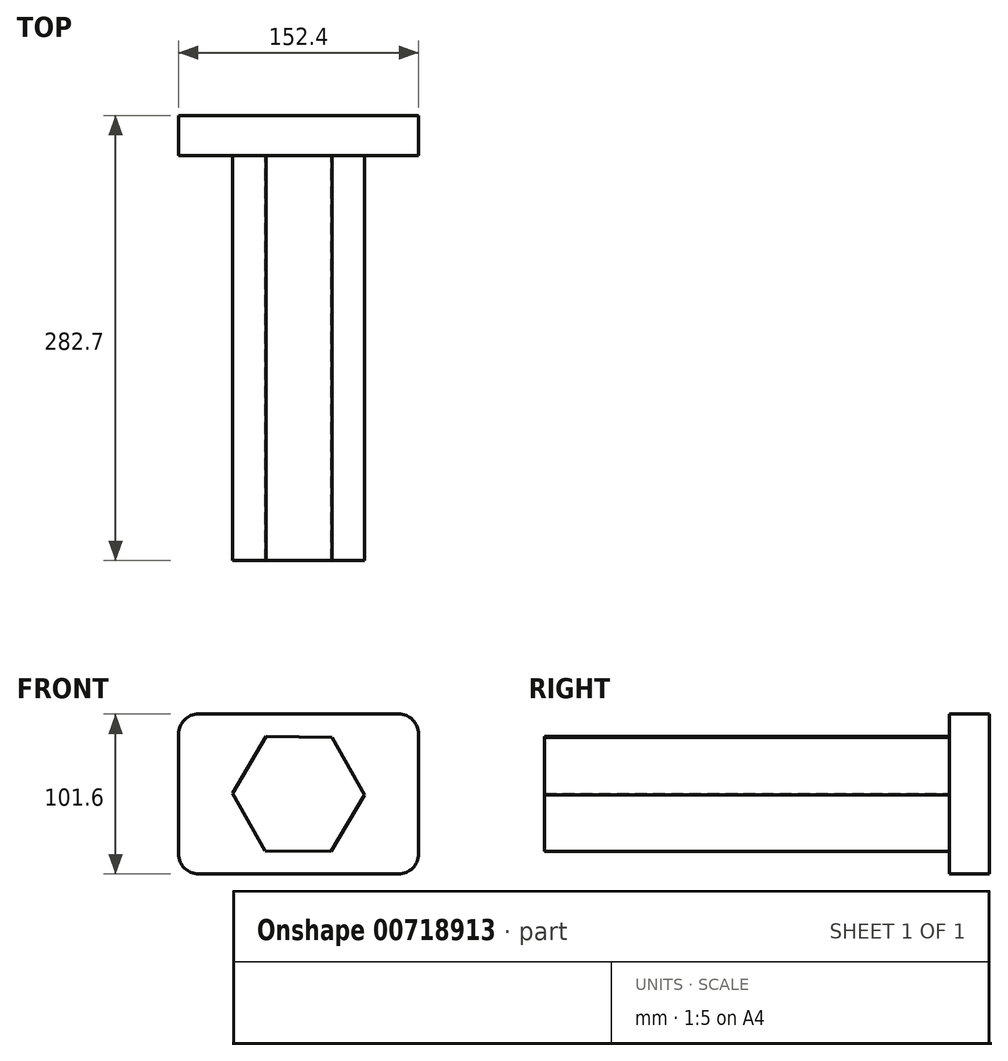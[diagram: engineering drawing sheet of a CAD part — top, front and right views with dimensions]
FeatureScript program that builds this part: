
annotation { "Feature Type Name" : "Feature", "Feature Type Description" : "" }
export const myFeature = defineFeature(function(context is Context, id is Id, definition is map)
    precondition{}
    {
        {
            var Q0;
            Q0=qCreatedBy(makeId("Front.planeOp"),FACE);
            var sketch = newSketch(context, id + "F0", { "sketchPlane" : qUnion([Q0])});
            skLineSegment(sketch, "E0.bottom", {"start": v(-83.42, -50.8) * mm, "end": v(43.58, -50.8) * mm});
            skLineSegment(sketch, "E0.top", {"start": v(-83.42, 50.8) * mm, "end": v(43.58, 50.8) * mm});
            skLineSegment(sketch, "E0.left", {"start": v(-96.12, -38.1) * mm, "end": v(-96.12, 38.1) * mm});
            skLineSegment(sketch, "E0.right", {"start": v(56.28, -38.1) * mm, "end": v(56.28, 38.1) * mm});
            skPoint(sketch, "E1.visualSharp", {"position": v(-96.12, 50.8) * mm});
            skArc(sketch, "E1.filletArc", {"start": v(-83.42, 50.8) * mm, "mid": v(-92.4, 47.08) * mm, "end": v(-96.12, 38.1) * mm});
            skPoint(sketch, "E2.visualSharp", {"position": v(-96.12, -50.8) * mm});
            skArc(sketch, "E2.filletArc", {"start": v(-96.12, -38.1) * mm, "mid": v(-92.4, -47.08) * mm, "end": v(-83.42, -50.8) * mm});
            skPoint(sketch, "E3.visualSharp", {"position": v(56.28, -50.8) * mm});
            skArc(sketch, "E3.filletArc", {"start": v(43.58, -50.8) * mm, "mid": v(52.56, -47.08) * mm, "end": v(56.28, -38.1) * mm});
            skPoint(sketch, "E4.visualSharp", {"position": v(56.28, 50.8) * mm});
            skArc(sketch, "E4.filletArc", {"start": v(56.28, 38.1) * mm, "mid": v(52.56, 47.08) * mm, "end": v(43.58, 50.8) * mm});
            skCircle(sketch, "E5.cCircle", {"center": v(-19.92, 0) * mm, "radius": 36.32 * mm, "construction": true});
            skLineSegment(sketch, "E5.0", {"start": v(-61.85, 0.46) * mm, "end": v(-40.48, 36.54) * mm});
            skLineSegment(sketch, "E5.1", {"start": v(-40.48, 36.54) * mm, "end": v(1.45, 36.08) * mm});
            skLineSegment(sketch, "E5.2", {"start": v(1.45, 36.08) * mm, "end": v(22.02, -0.46) * mm});
            skLineSegment(sketch, "E5.3", {"start": v(22.02, -0.46) * mm, "end": v(0.65, -36.54) * mm});
            skLineSegment(sketch, "E5.4", {"start": v(0.65, -36.54) * mm, "end": v(-41.28, -36.08) * mm});
            skLineSegment(sketch, "E5.5", {"start": v(-41.28, -36.08) * mm, "end": v(-61.85, 0.46) * mm});
            skPoint(sketch, "E5.0.midPoint", {"position": v(-51.16, 18.5) * mm});
            skSolve(sketch);
        }
        {
            var Q0;
            Q0 = qSketchRegion(id + "F0", true);
            extrude(context, id + "F1", {"entities" : qUnion([Q0]), "depth" : 25.4 * mm, "offsetDistance" : 25.4 * mm});
        }
        {
            var Q0;
            Q0=makeQuery(id+"F0.imprint","IMPRINT",FACE,{"disambiguationData":[TD([[makeQuery(id+"F0.imprint","IMPRINT",EDGE,{"derivedFrom":sQuery(id+"F0.wireOp",EDGE,"E5.0")}),-1.0]])]});
            extrude(context, id + "F2", {"entities" : qUnion([Q0]), "operationType" : NewBodyOperationType.ADD, "depth" : 282.7 * mm, "offsetDistance" : 25.4 * mm});
        }
    });
